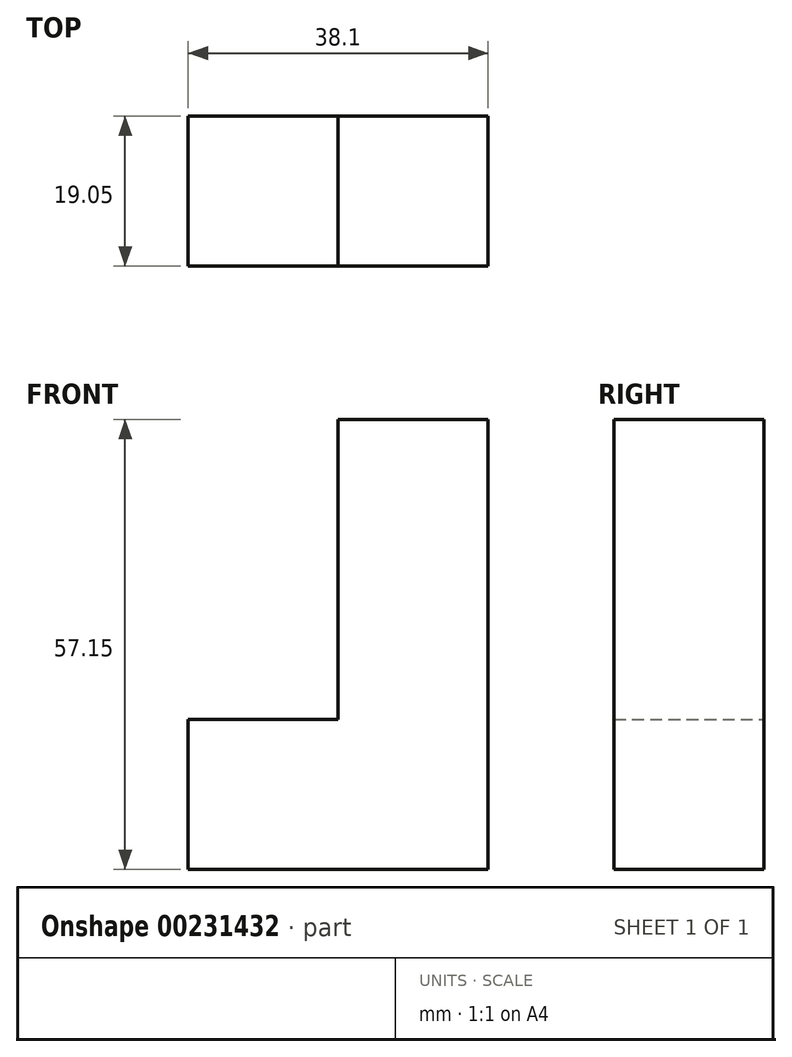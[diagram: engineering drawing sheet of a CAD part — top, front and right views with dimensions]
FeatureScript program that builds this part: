
annotation { "Feature Type Name" : "Feature", "Feature Type Description" : "" }
export const myFeature = defineFeature(function(context is Context, id is Id, definition is map)
    precondition{}
    {
        {
            var Q0;
            Q0=qCreatedBy(makeId("Front.planeOp"),FACE);
            var sketch = newSketch(context, id + "F0", { "sketchPlane" : qUnion([Q0])});
            skLineSegment(sketch, "E0.bottom", {"start": v(-47.7, 43.24) * mm, "end": v(-28.65, 43.24) * mm});
            skLineSegment(sketch, "E0.top", {"start": v(-47.7, -13.91) * mm, "end": v(-28.65, -13.91) * mm});
            skLineSegment(sketch, "E0.left", {"start": v(-47.7, 43.24) * mm, "end": v(-47.7, -13.91) * mm});
            skLineSegment(sketch, "E0.right", {"start": v(-28.65, 43.24) * mm, "end": v(-28.65, -13.91) * mm});
            skLineSegment(sketch, "E1.bottom", {"start": v(-66.75, 5.14) * mm, "end": v(-47.7, 5.14) * mm});
            skLineSegment(sketch, "E1.top", {"start": v(-66.75, -13.91) * mm, "end": v(-47.7, -13.91) * mm});
            skLineSegment(sketch, "E1.left", {"start": v(-66.75, 5.14) * mm, "end": v(-66.75, -13.91) * mm});
            skLineSegment(sketch, "E1.right", {"start": v(-47.7, 5.14) * mm, "end": v(-47.7, -13.91) * mm});
            skSolve(sketch);
        }
        {
            var Q0;
            Q0 = qSketchRegion(id + "F0", true);
            extrude(context, id + "F1", {"entities" : qUnion([Q0]), "depth" : 19.05 * mm});
        }
    });
